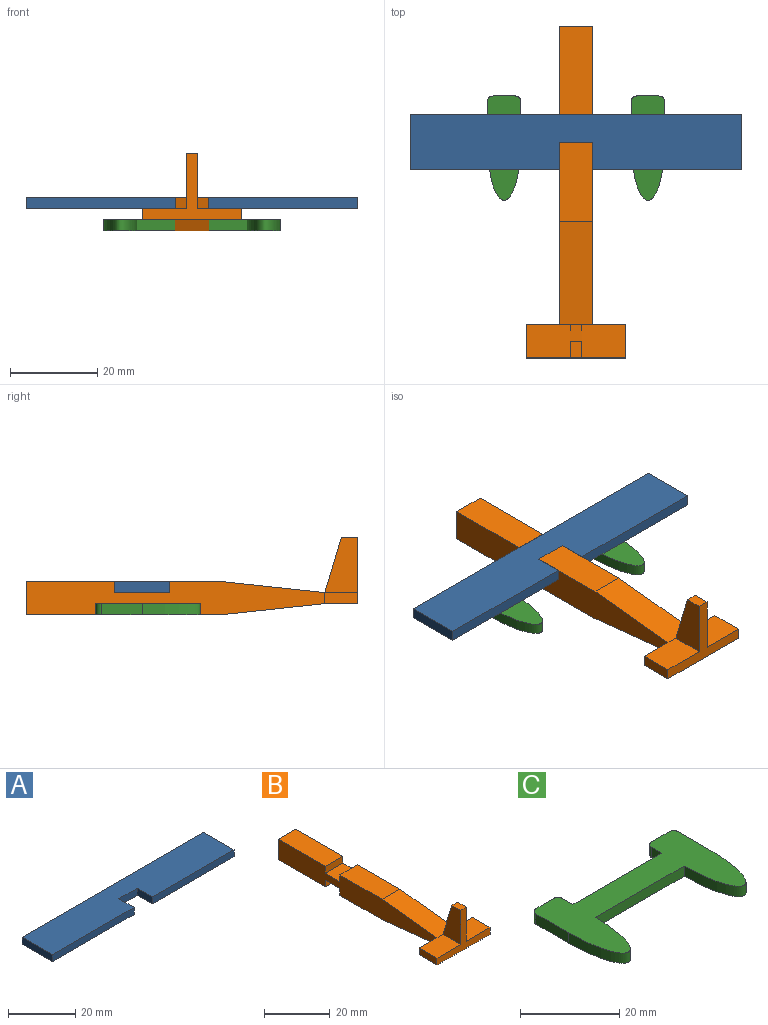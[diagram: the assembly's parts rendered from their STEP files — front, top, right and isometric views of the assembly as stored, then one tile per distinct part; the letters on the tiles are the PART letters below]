
ASSEMBLY  parts=3 mates=2
PART A: 10 faces, bbox 76.2x12.7x2.5 mm
  f0: plane 34.29x2.54mm, normal (0,-1,0), area 87.1mm2, adj f1,f4,f6,f7
  f1: plane 76.2x12.7mm, normal (0,0,-1), area 919.4mm2, adj f0,f2,f3,f4,f5,f7,f8,f9
  f2: plane 12.7x2.54mm, normal (-1,0,0), area 32.3mm2, adj f1,f3,f5,f6
  f3: plane 34.29x2.54mm, normal (0,-1,0), area 87.1mm2, adj f1,f2,f6,f9
  f4: plane 12.7x2.54mm, normal (1,0,0), area 32.3mm2, adj f0,f1,f5,f6
  f5: plane 76.2x2.54mm, normal (0,1,0), area 193.5mm2, adj f1,f2,f4,f6
  f6: plane 76.2x12.7mm, normal (0,0,1), area 919.4mm2, adj f0,f2,f3,f4,f5,f7,f8,f9
  f7: plane 6.35x2.54mm, normal (-1,0,0), area 16.1mm2, adj f0,f1,f6,f8
  f8: plane 7.62x2.54mm, normal (0,-1,0), area 19.4mm2, adj f1,f6,f7,f9
  f9: plane 6.35x2.54mm, normal (1,0,0), area 16.1mm2, adj f1,f3,f6,f8
PART B: 27 faces, bbox 22.9x76.2x17.8 mm
  f0: plane 3.81x2.54mm, normal (0,0,1), area 9.7mm2, adj f3,f22,f23,f26
  f1: plane 68.58x7.62mm, normal (1,0,0), area 430.2mm2, adj f4,f5,f6,f7,f8,f9,f10,f11
  f2: plane 68.58x7.62mm, normal (-1,0,0), area 430.2mm2, adj f4,f5,f6,f7,f8,f9,f10,f11
  f3: plane 22.86x15.24mm, normal (0,-1,0), area 90.3mm2, adj f0,f15,f16,f19,f20,f21,f22,f23
  f4: plane 18.23x7.62mm, normal (0,0,1), area 138.9mm2, adj f1,f2,f11,f25
  f5: plane 18.23x7.62mm, normal (0,0,-1), area 138.9mm2, adj f1,f2,f14,f24
  f6: plane 7.62x6.35mm, normal (0,0,-1), area 48.4mm2, adj f1,f2,f12,f14
  f7: plane 7.62x6.35mm, normal (0,0,1), area 48.4mm2, adj f1,f2,f9,f11
  f8: plane 7.62x7.62mm, normal (0,1,0), area 58.1mm2, adj f1,f2,f10,f13
  f9: plane 7.62x2.54mm, normal (0,-1,0), area 19.4mm2, adj f1,f2,f7,f10
  f10: plane 20.32x7.62mm, normal (0,0,1), area 154.8mm2, adj f1,f2,f8,f9
  f11: plane 7.62x2.54mm, normal (0,1,0), area 19.4mm2, adj f1,f2,f4,f7
  f12: plane 7.62x2.54mm, normal (0,-1,0), area 19.4mm2, adj f1,f2,f6,f13
  f13: plane 20.32x7.62mm, normal (0,0,-1), area 154.8mm2, adj f1,f2,f8,f12
  f14: plane 7.62x2.54mm, normal (0,1,0), area 19.4mm2, adj f1,f2,f5,f6
  f15: plane 7.62x2.54mm, normal (1,0,0), area 19.4mm2, adj f3,f16,f17,f20
  f16: plane 10.16x7.62mm, normal (0,0,1), area 77.4mm2, adj f3,f15,f17,f23,f25
  f17: plane 7.62x2.54mm, normal (0,1,0), area 19.4mm2, adj f1,f15,f16,f20
  f18: plane 7.62x2.54mm, normal (0,1,0), area 19.4mm2, adj f2,f19,f20,f21
  f19: plane 10.16x7.62mm, normal (0,0,1), area 77.4mm2, adj f3,f18,f21,f22,f25
  f20: plane 22.86x7.62mm, normal (0,0,-1), area 174.2mm2, adj f3,f15,f17,f18,f21,f24
  f21: plane 7.62x2.54mm, normal (-1,0,0), area 19.4mm2, adj f3,f18,f19,f20
  f22: plane 12.7x7.62mm, normal (-1,0,0), area 72.6mm2, adj f0,f3,f19,f26
  f23: plane 12.7x7.62mm, normal (1,0,0), area 72.6mm2, adj f0,f3,f16,f26
  f24: plane 23.68x7.62mm, normal (0,-0.11,-0.99), area 181.5mm2, adj f1,f2,f5,f20
  f25: plane 23.68x7.62mm, normal (0,-0.11,0.99), area 181.5mm2, adj f1,f2,f4,f16,f19,f26
  f26: plane 12.7x3.81mm, normal (0,0.96,0.29), area 33.7mm2, adj f0,f22,f23,f25
PART C: 16 faces, bbox 40.6x23.9x2.5 mm
  f0: plane 25.4x2.54mm, normal (0,1,0), area 64.5mm2, adj f1,f13,f14,f15
  f1: plane 2.99x2.54mm, normal (1,0,0), area 7.6mm2, adj f0,f2,f14,f15
  f2: cylinder r=1.27mm len=2.54mm, axis (0,0,-1), area 5.1mm2, adj f1,f3,f14,f15
  f3: plane 5.08x2.54mm, normal (0,1,0), area 12.9mm2, adj f2,f4,f14,f15
  f4: cylinder r=1.27mm len=2.54mm, axis (0,0,-1), area 5.1mm2, adj f3,f5,f14,f15
  f5: plane 9.34x2.54mm, normal (-1,0,0), area 23.7mm2, adj f4,f6,f14,f15
  f6: extruded ~13.34x7.62mm, area 73.8mm2, adj f5,f7,f14,f15
  f7: plane 25.4x2.54mm, normal (0,-1,0), area 64.5mm2, adj f6,f8,f14,f15
  f8: extruded ~13.34x7.62mm, area 73.8mm2, adj f7,f9,f14,f15
  f9: plane 9.34x2.54mm, normal (1,0,0), area 23.7mm2, adj f8,f10,f14,f15
  f10: cylinder r=1.27mm len=2.54mm, axis (0,0,-1), area 5.1mm2, adj f9,f11,f14,f15
  f11: plane 5.08x2.54mm, normal (0,1,0), area 12.9mm2, adj f10,f12,f14,f15
  f12: cylinder r=1.27mm len=2.54mm, axis (0,0,-1), area 5.1mm2, adj f11,f13,f14,f15
  f13: plane 2.99x2.54mm, normal (-1,0,0), area 7.6mm2, adj f0,f12,f14,f15
  f14: plane 40.64x23.95mm, normal (0,0,1), area 481.2mm2, adj f0,f1,f2,f3,f4,f5,f6,f7
  f15: plane 40.64x23.95mm, normal (0,0,-1), area 481.2mm2, adj f0,f1,f2,f3,f4,f5,f6,f7
PLACE A t=(59.92,28.74,2.54)mm
PLACE B at identity fixed
PLACE C t=(-37.62,0.74,-2.54)mm
MATE fastened B.f7 <-> A.f1  axis (0,0,1) through (21.82,41.44,2.54)mm
MATE fastened B.f6 <-> C.f14  axis (0,0,-1) through (21.82,41.44,0)mm
